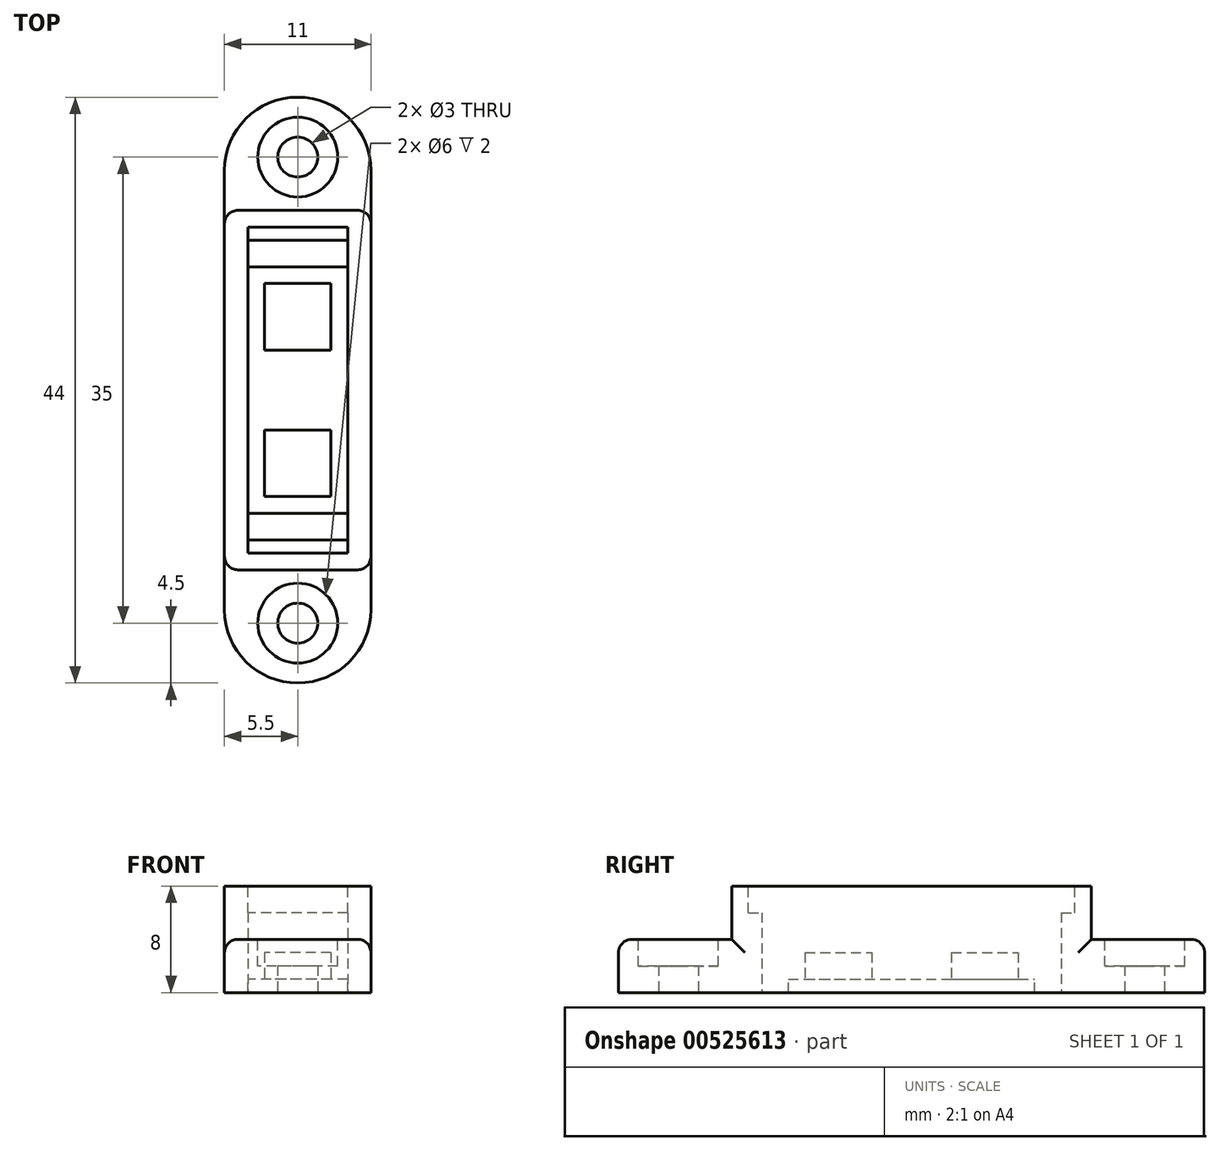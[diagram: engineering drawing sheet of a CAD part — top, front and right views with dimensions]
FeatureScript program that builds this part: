
annotation { "Feature Type Name" : "Feature", "Feature Type Description" : "" }
export const myFeature = defineFeature(function(context is Context, id is Id, definition is map)
    precondition{}
    {
        {
            var Q0;
            Q0=qCreatedBy(makeId("Top.planeOp"),FACE);
            var sketch = newSketch(context, id + "F0", { "sketchPlane" : qUnion([Q0])});
            skLineSegment(sketch, "E0.bottom", {"start": v(5.5, -16.5) * mm, "end": v(-5.5, -16.5) * mm});
            skLineSegment(sketch, "E0.top", {"start": v(5.5, 16.5) * mm, "end": v(-5.5, 16.5) * mm});
            skLineSegment(sketch, "E0.left", {"start": v(5.5, -16.5) * mm, "end": v(5.5, 16.5) * mm});
            skLineSegment(sketch, "E0.right", {"start": v(-5.5, -16.5) * mm, "end": v(-5.5, 16.5) * mm});
            skPoint(sketch, "E0.middle", {"position": v(0, 0) * mm});
            skCircle(sketch, "E1", {"center": v(0, 17.5) * mm, "radius": 1.5 * mm});
            skCircle(sketch, "E2", {"center": v(0, -17.5) * mm, "radius": 1.5 * mm});
            skArc(sketch, "E3", {"start": v(-5.5, -16.5) * mm, "mid": v(0, -22) * mm, "end": v(5.5, -16.5) * mm});
            skArc(sketch, "E4", {"start": v(5.5, 16.5) * mm, "mid": v(0, 22) * mm, "end": v(-5.5, 16.5) * mm});
            skSolve(sketch);
        }
        {
            var Q0;
            Q0 = qSketchRegion(id + "F0", true);
            extrude(context, id + "F1", {"entities" : qUnion([Q0]), "depth" : 4 * mm, "offsetDistance" : 25 * mm});
        }
        {
            var Q0;
            Q0=makeQuery(id+"F1.opExtrude","CAP_FACE",FACE,{"disambiguationData":[OSD([sQuery(id+"F0.wireOp",EDGE,"E0.bottom"),sQuery(id+"F0.wireOp",EDGE,"E0.top"),sQuery(id+"F0.wireOp",EDGE,"E0.left"),sQuery(id+"F0.wireOp",EDGE,"E0.right"),sQuery(id+"F0.wireOp",EDGE,"E1"),sQuery(id+"F0.wireOp",EDGE,"E2")])],"isStart":false});
            var sketch = newSketch(context, id + "F2", { "sketchPlane" : qUnion([Q0])});
            skLineSegment(sketch, "E5.bottom", {"start": v(5.5, -13.5) * mm, "end": v(-5.5, -13.5) * mm});
            skLineSegment(sketch, "E5.top", {"start": v(5.5, 13.5) * mm, "end": v(-5.5, 13.5) * mm});
            skLineSegment(sketch, "E5.left", {"start": v(5.5, -13.5) * mm, "end": v(5.5, 13.5) * mm});
            skLineSegment(sketch, "E5.right", {"start": v(-5.5, -13.5) * mm, "end": v(-5.5, 13.5) * mm});
            skPoint(sketch, "E5.middle", {"position": v(0, 0) * mm});
            skSolve(sketch);
        }
        {
            var Q0;
            Q0 = qSketchRegion(id + "F2", true);
            extrude(context, id + "F3", {"entities" : qUnion([Q0]), "operationType" : NewBodyOperationType.ADD, "depth" : 4 * mm, "offsetDistance" : 25 * mm});
        }
        {
            var Q0;
            Q0=makeQuery(id+"F3.opExtrude","CAP_FACE",FACE,{"disambiguationData":[OSD([sQuery(id+"F2.wireOp",EDGE,"E5.bottom"),sQuery(id+"F2.wireOp",EDGE,"E5.top"),sQuery(id+"F2.wireOp",EDGE,"E5.left"),sQuery(id+"F2.wireOp",EDGE,"E5.right")])],"isStart":false});
            var sketch = newSketch(context, id + "F4", { "sketchPlane" : qUnion([Q0])});
            skLineSegment(sketch, "E6.bottom", {"start": v(3.75, -12.25) * mm, "end": v(-3.75, -12.25) * mm});
            skLineSegment(sketch, "E6.top", {"start": v(3.75, 12.25) * mm, "end": v(-3.75, 12.25) * mm});
            skLineSegment(sketch, "E6.left", {"start": v(3.75, -12.25) * mm, "end": v(3.75, 12.25) * mm});
            skLineSegment(sketch, "E6.right", {"start": v(-3.75, -12.25) * mm, "end": v(-3.75, 12.25) * mm});
            skPoint(sketch, "E6.middle", {"position": v(0, 0) * mm});
            skSolve(sketch);
        }
        {
            var Q0;
            Q0 = qSketchRegion(id + "F4", true);
            extrude(context, id + "F5", {"entities" : qUnion([Q0]), "operationType" : NewBodyOperationType.REMOVE, "oppositeDirection" : true, "depth" : 7 * mm, "offsetDistance" : 25 * mm});
        }
        {
            var Q0;
            Q0=makeQuery(id+"F5.boolean.opBoolean","COPY",FACE,{"derivedFrom":makeQuery(id+"F5.opExtrude","CAP_FACE",FACE,{"disambiguationData":[OSD([sQuery(id+"F4.wireOp",EDGE,"E6.bottom"),sQuery(id+"F4.wireOp",EDGE,"E6.top"),sQuery(id+"F4.wireOp",EDGE,"E6.left"),sQuery(id+"F4.wireOp",EDGE,"E6.right")])],"isStart":false})});
            var sketch = newSketch(context, id + "F6", { "sketchPlane" : qUnion([Q0])});
            skLineSegment(sketch, "E7.bottom", {"start": v(-3.75, 12.25) * mm, "end": v(3.75, 12.25) * mm});
            skLineSegment(sketch, "E7.top", {"start": v(-3.75, 11.25) * mm, "end": v(3.75, 11.25) * mm});
            skLineSegment(sketch, "E7.left", {"start": v(-3.75, 12.25) * mm, "end": v(-3.75, 11.25) * mm});
            skLineSegment(sketch, "E7.right", {"start": v(3.75, 12.25) * mm, "end": v(3.75, 11.25) * mm});
            skLineSegment(sketch, "E8.bottom", {"start": v(3.75, -12.25) * mm, "end": v(-3.75, -12.25) * mm});
            skLineSegment(sketch, "E8.top", {"start": v(3.75, -11.25) * mm, "end": v(-3.75, -11.25) * mm});
            skLineSegment(sketch, "E8.left", {"start": v(3.75, -12.25) * mm, "end": v(3.75, -11.25) * mm});
            skLineSegment(sketch, "E8.right", {"start": v(-3.75, -12.25) * mm, "end": v(-3.75, -11.25) * mm});
            skSolve(sketch);
        }
        {
            var Q0;
            Q0 = qSketchRegion(id + "F6", true);
            extrude(context, id + "F7", {"entities" : qUnion([Q0]), "operationType" : NewBodyOperationType.ADD, "depth" : 5 * mm, "offsetDistance" : 25 * mm});
        }
        {
            var Q0;
            Q0=makeQuery(id+"F5.boolean.opBoolean","COPY",FACE,{"derivedFrom":makeQuery(id+"F5.opExtrude","CAP_FACE",FACE,{"disambiguationData":[OSD([sQuery(id+"F4.wireOp",EDGE,"E6.bottom"),sQuery(id+"F4.wireOp",EDGE,"E6.top"),sQuery(id+"F4.wireOp",EDGE,"E6.left"),sQuery(id+"F4.wireOp",EDGE,"E6.right")])],"isStart":false})});
            var sketch = newSketch(context, id + "F8", { "sketchPlane" : qUnion([Q0])});
            skLineSegment(sketch, "E9.bottom", {"start": v(3.75, 9.25) * mm, "end": v(-3.75, 9.25) * mm});
            skLineSegment(sketch, "E9.top", {"start": v(3.75, 11.25) * mm, "end": v(-3.75, 11.25) * mm});
            skLineSegment(sketch, "E9.left", {"start": v(3.75, 9.25) * mm, "end": v(3.75, 11.25) * mm});
            skLineSegment(sketch, "E9.right", {"start": v(-3.75, 9.25) * mm, "end": v(-3.75, 11.25) * mm});
            skPoint(sketch, "E9.middle", {"position": v(0, 10.25) * mm});
            skLineSegment(sketch, "E10.bottom", {"start": v(3.75, -11.25) * mm, "end": v(-3.75, -11.25) * mm});
            skLineSegment(sketch, "E10.top", {"start": v(3.75, -9.25) * mm, "end": v(-3.75, -9.25) * mm});
            skLineSegment(sketch, "E10.left", {"start": v(3.75, -11.25) * mm, "end": v(3.75, -9.25) * mm});
            skLineSegment(sketch, "E10.right", {"start": v(-3.75, -11.25) * mm, "end": v(-3.75, -9.25) * mm});
            skPoint(sketch, "E10.middle", {"position": v(0, -10.25) * mm});
            skSolve(sketch);
        }
        {
            var Q0;
            Q0 = qSketchRegion(id + "F8", true);
            extrude(context, id + "F9", {"entities" : qUnion([Q0]), "operationType" : NewBodyOperationType.REMOVE, "oppositeDirection" : true, "depth" : 25 * mm, "offsetDistance" : 25 * mm});
        }
        {
            var Q0;
            Q0=makeQuery(id+"F5.boolean.opBoolean","COPY",FACE,{"derivedFrom":makeQuery(id+"F5.opExtrude","CAP_FACE",FACE,{"disambiguationData":[OSD([sQuery(id+"F4.wireOp",EDGE,"E6.bottom"),sQuery(id+"F4.wireOp",EDGE,"E6.top"),sQuery(id+"F4.wireOp",EDGE,"E6.left"),sQuery(id+"F4.wireOp",EDGE,"E6.right")])],"isStart":false})});
            var sketch = newSketch(context, id + "F10", { "sketchPlane" : qUnion([Q0])});
            skLineSegment(sketch, "E11.bottom", {"start": v(2.5, 3) * mm, "end": v(-2.5, 3) * mm});
            skLineSegment(sketch, "E11.top", {"start": v(2.5, 8) * mm, "end": v(-2.5, 8) * mm});
            skLineSegment(sketch, "E11.left", {"start": v(2.5, 3) * mm, "end": v(2.5, 8) * mm});
            skLineSegment(sketch, "E11.right", {"start": v(-2.5, 3) * mm, "end": v(-2.5, 8) * mm});
            skPoint(sketch, "E11.middle", {"position": v(0, 5.5) * mm});
            skLineSegment(sketch, "E12.bottom", {"start": v(2.5, -8) * mm, "end": v(-2.5, -8) * mm});
            skLineSegment(sketch, "E12.top", {"start": v(2.5, -3) * mm, "end": v(-2.5, -3) * mm});
            skLineSegment(sketch, "E12.left", {"start": v(2.5, -8) * mm, "end": v(2.5, -3) * mm});
            skLineSegment(sketch, "E12.right", {"start": v(-2.5, -8) * mm, "end": v(-2.5, -3) * mm});
            skPoint(sketch, "E12.middle", {"position": v(0, -5.5) * mm});
            skSolve(sketch);
        }
        {
            var Q0;
            Q0 = qSketchRegion(id + "F10", true);
            extrude(context, id + "F11", {"entities" : qUnion([Q0]), "depth" : 2 * mm, "offsetDistance" : 25 * mm});
        }
        {
            var Q0;
            {var subQ0=sQuery(id+"F0.wireOp",EDGE,"E4");var subQ1=sQuery(id+"F0.wireOp",EDGE,"E1");var subQ2=sQuery(id+"F0.wireOp",EDGE,"E0.right");var subQ3=sQuery(id+"F0.wireOp",EDGE,"E0.left");Q0=makeQuery(id+"F3.boolean.opBoolean","SPLIT",FACE,{"disambiguationData":[TD([makeQuery(id+"F1.opExtrude","SWEPT_FACE",FACE,{"disambiguationData":[OSD([subQ1])]})])],"derivedFrom":makeQuery(id+"F1.opExtrude","CAP_FACE",FACE,{"disambiguationData":[OSD([subQ3,subQ2,subQ1,sQuery(id+"F0.wireOp",EDGE,"E2"),sQuery(id+"F0.wireOp",EDGE,"E3"),subQ0])],"isStart":false})});}
            var sketch = newSketch(context, id + "F12", { "sketchPlane" : qUnion([Q0])});
            skCircle(sketch, "E13", {"center": v(0, 17.5) * mm, "radius": 3 * mm});
            skCircle(sketch, "E14", {"center": v(0, -17.5) * mm, "radius": 3 * mm});
            skCircle(sketch, "E15.0", {"center": v(0, -17.5) * mm, "radius": 1.5 * mm});
            skSolve(sketch);
        }
        {
            var Q0;
            Q0 = qSketchRegion(id + "F12", true);
            extrude(context, id + "F13", {"entities" : qUnion([Q0]), "operationType" : NewBodyOperationType.REMOVE, "oppositeDirection" : true, "depth" : 2 * mm, "offsetDistance" : 25 * mm});
        }
        {
            var Q0;
            Q0=makeQuery(id+"F1.opExtrude","CAP_EDGE",EDGE,{"disambiguationData":[OSD([sQuery(id+"F0.wireOp",EDGE,"E3")])],"isStart":false});
            var Q1;
            Q1=makeQuery(id+"F1.opExtrude","CAP_EDGE",EDGE,{"disambiguationData":[OSD([sQuery(id+"F0.wireOp",EDGE,"SditnZvs-4hyL-ZjZA-GRju-Q3q02jCkBATM")])],"isStart":false});
            var Q2;
            Q2=makeQuery(id+"F3.opExtrude","SWEPT_EDGE",EDGE,{"disambiguationData":[OSD([sQuery(id+"F0.wireOp",EDGE,"E0.right"),sQuery(id+"F2.wireOp",EDGE,"E5.bottom"),sQuery(id+"F2.wireOp",EDGE,"E5.right")])]});
            var Q3;
            Q3=makeQuery(id+"F3.opExtrude","SWEPT_EDGE",EDGE,{"disambiguationData":[OSD([sQuery(id+"F0.wireOp",EDGE,"E0.left"),sQuery(id+"F2.wireOp",EDGE,"E5.bottom"),sQuery(id+"F2.wireOp",EDGE,"E5.left")])]});
            var Q4;
            Q4=makeQuery(id+"F3.opExtrude","SWEPT_EDGE",EDGE,{"disambiguationData":[OSD([sQuery(id+"F0.wireOp",EDGE,"E0.left"),sQuery(id+"F2.wireOp",EDGE,"E5.top"),sQuery(id+"F2.wireOp",EDGE,"E5.left")])]});
            var Q5;
            Q5=makeQuery(id+"F3.opExtrude","SWEPT_EDGE",EDGE,{"disambiguationData":[OSD([sQuery(id+"F0.wireOp",EDGE,"E0.right"),sQuery(id+"F2.wireOp",EDGE,"E5.top"),sQuery(id+"F2.wireOp",EDGE,"E5.right")])]});
            var Q6;
            Q6=makeQuery(id+"F1.opExtrude","CAP_EDGE",EDGE,{"disambiguationData":[OSD([sQuery(id+"F0.wireOp",EDGE,"E4")])],"isStart":false});
            fillet(context, id + "F14", {"entities" : qUnion([Q0, Q1, Q2, Q3, Q4, Q5, Q6]), "radius" : 1 * mm, "tangentPropagation" : true, "allowEdgeOverflow" : false});
        }
    });
